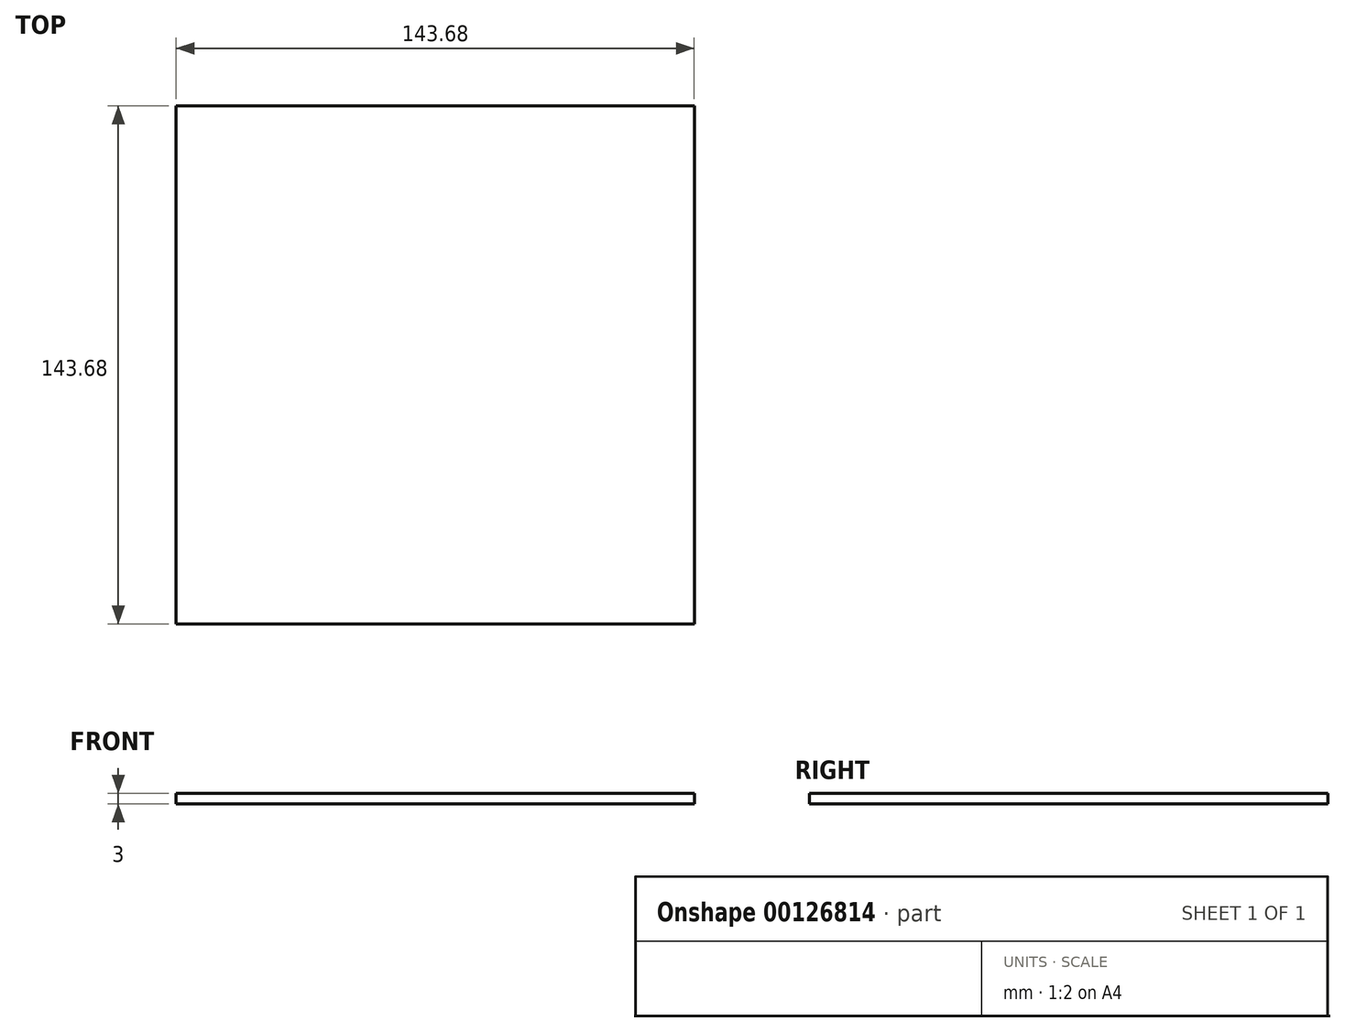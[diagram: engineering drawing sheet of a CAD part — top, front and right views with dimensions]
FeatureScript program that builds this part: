
annotation { "Feature Type Name" : "Feature", "Feature Type Description" : "" }
export const myFeature = defineFeature(function(context is Context, id is Id, definition is map)
    precondition{}
    {
        {
            var Q0;
            Q0=qCreatedBy(makeId("Top.planeOp"),FACE);
            var sketch = newSketch(context, id + "F0", { "sketchPlane" : qUnion([Q0])});
            skLineSegment(sketch, "E0", {"start": v(-137.27, 66.6) * mm, "end": v(-137.27, -77.08) * mm});
            skLineSegment(sketch, "E1", {"start": v(-137.27, 66.6) * mm, "end": v(6.41, 66.6) * mm});
            skLineSegment(sketch, "E2", {"start": v(-137.27, -77.08) * mm, "end": v(6.41, -77.08) * mm});
            skLineSegment(sketch, "E3", {"start": v(6.41, -77.08) * mm, "end": v(6.41, 66.6) * mm});
            skLineSegment(sketch, "E4", {"start": v(-137.27, 66.6) * mm, "end": v(6.41, -77.08) * mm, "construction": true});
            skLineSegment(sketch, "E5", {"start": v(-137.27, -77.08) * mm, "end": v(6.41, 66.6) * mm, "construction": true});
            skPoint(sketch, "E6", {"position": v(-65.43, -5.24) * mm});
            skCircle(sketch, "E7", {"center": v(-65.43, -5.24) * mm, "radius": 101.6 * mm, "construction": true});
            skLineSegment(sketch, "E8", {"start": v(-65.43, -5.24) * mm, "end": v(-167.03, -5.24) * mm, "construction": true});
            skLineSegment(sketch, "E9", {"start": v(-65.43, -5.24) * mm, "end": v(36.17, -5.24) * mm, "construction": true});
            skSolve(sketch);
        }
        {
            var Q0;
            Q0=makeQuery(id+"F0.imprint","IMPRINT",FACE,{"disambiguationData":[TD([[makeQuery(id+"F0.imprint","IMPRINT",EDGE,{"derivedFrom":sQuery(id+"F0.wireOp",EDGE,"E0")}),1.0]])]});
            extrude(context, id + "F1", {"entities" : qUnion([Q0]), "depth" : 3 * mm});
        }
    });
